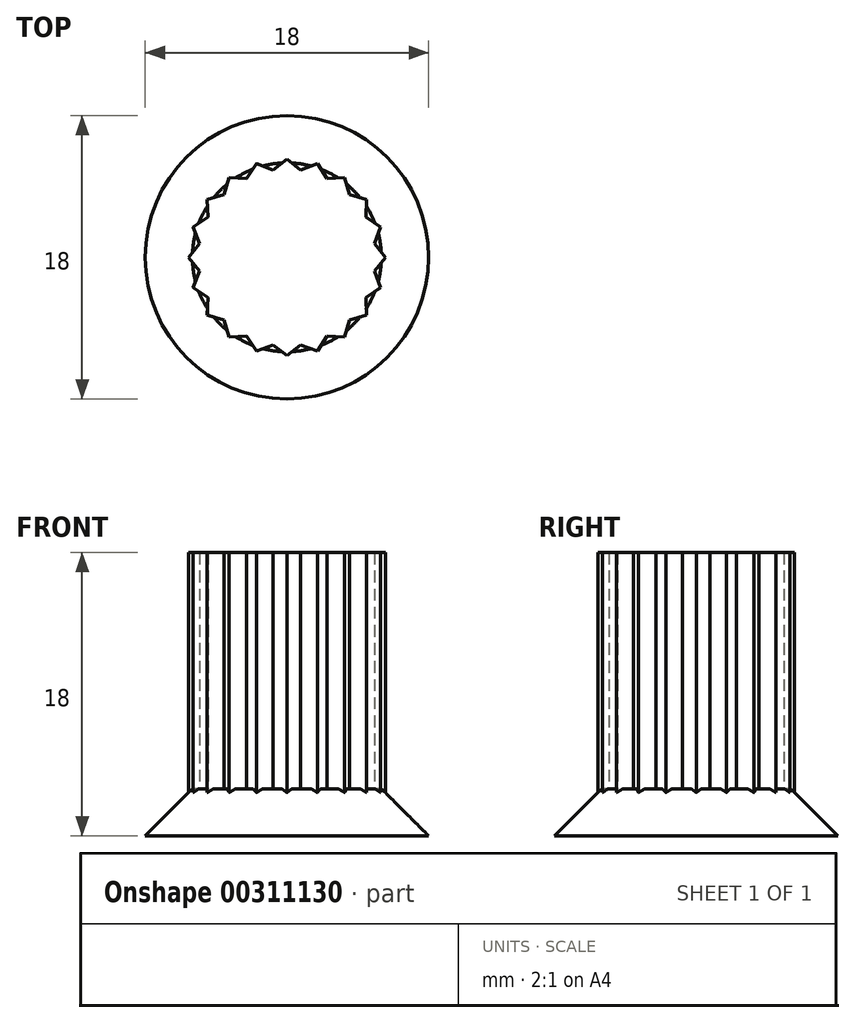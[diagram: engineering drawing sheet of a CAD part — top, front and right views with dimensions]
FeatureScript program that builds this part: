
annotation { "Feature Type Name" : "Feature", "Feature Type Description" : "" }
export const myFeature = defineFeature(function(context is Context, id is Id, definition is map)
    precondition{}
    {
        {
            var Q0;
            Q0=qCreatedBy(makeId("Top.planeOp"),FACE);
            var sketch = newSketch(context, id + "F0", { "sketchPlane" : qUnion([Q0])});
            skArc(sketch, "E0", {"start": v(0, 9) * mm, "mid": v(-6.36, 6.36) * mm, "end": v(-9, 0) * mm});
            skArc(sketch, "E1", {"start": v(-9, 0) * mm, "mid": v(-6.36, -6.36) * mm, "end": v(0, -9) * mm});
            skArc(sketch, "E2", {"start": v(0, -9) * mm, "mid": v(6.36, -6.36) * mm, "end": v(9, 0) * mm});
            skArc(sketch, "E3", {"start": v(9, 0) * mm, "mid": v(6.36, 6.36) * mm, "end": v(0, 9) * mm});
            skLineSegment(sketch, "E4", {"start": v(0.88, 5.56) * mm, "end": v(0, 6.25) * mm});
            skLineSegment(sketch, "E5", {"start": v(0, 6.25) * mm, "end": v(-0.88, 5.56) * mm});
            skLineSegment(sketch, "E6", {"start": v(-0.88, 5.56) * mm, "end": v(-1.93, 5.94) * mm});
            skLineSegment(sketch, "E7", {"start": v(-1.93, 5.94) * mm, "end": v(-2.55, 5.01) * mm});
            skLineSegment(sketch, "E8", {"start": v(-2.55, 5.01) * mm, "end": v(-3.67, 5.06) * mm});
            skLineSegment(sketch, "E9", {"start": v(-3.67, 5.06) * mm, "end": v(-3.98, 3.98) * mm});
            skLineSegment(sketch, "E10", {"start": v(-3.98, 3.98) * mm, "end": v(-5.06, 3.67) * mm});
            skLineSegment(sketch, "E11", {"start": v(-5.06, 3.67) * mm, "end": v(-5.01, 2.55) * mm});
            skLineSegment(sketch, "E12", {"start": v(-5.01, 2.55) * mm, "end": v(-5.94, 1.93) * mm});
            skLineSegment(sketch, "E13", {"start": v(-5.94, 1.93) * mm, "end": v(-5.56, 0.88) * mm});
            skLineSegment(sketch, "E14", {"start": v(-5.56, 0.88) * mm, "end": v(-6.25, 0) * mm});
            skLineSegment(sketch, "E15", {"start": v(-6.25, 0) * mm, "end": v(-5.56, -0.88) * mm});
            skLineSegment(sketch, "E16", {"start": v(-5.56, -0.88) * mm, "end": v(-5.94, -1.93) * mm});
            skLineSegment(sketch, "E17", {"start": v(-5.94, -1.93) * mm, "end": v(-5.01, -2.55) * mm});
            skLineSegment(sketch, "E18", {"start": v(-5.01, -2.55) * mm, "end": v(-5.06, -3.67) * mm});
            skLineSegment(sketch, "E19", {"start": v(-5.06, -3.67) * mm, "end": v(-3.98, -3.98) * mm});
            skLineSegment(sketch, "E20", {"start": v(-3.98, -3.98) * mm, "end": v(-3.67, -5.06) * mm});
            skLineSegment(sketch, "E21", {"start": v(-3.67, -5.06) * mm, "end": v(-2.55, -5.01) * mm});
            skLineSegment(sketch, "E22", {"start": v(-2.55, -5.01) * mm, "end": v(-1.93, -5.94) * mm});
            skLineSegment(sketch, "E23", {"start": v(-1.93, -5.94) * mm, "end": v(-0.88, -5.56) * mm});
            skLineSegment(sketch, "E24", {"start": v(-0.88, -5.56) * mm, "end": v(0, -6.25) * mm});
            skLineSegment(sketch, "E25", {"start": v(0, -6.25) * mm, "end": v(0.88, -5.56) * mm});
            skLineSegment(sketch, "E26", {"start": v(0.88, -5.56) * mm, "end": v(1.93, -5.94) * mm});
            skLineSegment(sketch, "E27", {"start": v(1.93, -5.94) * mm, "end": v(2.55, -5.01) * mm});
            skLineSegment(sketch, "E28", {"start": v(2.55, -5.01) * mm, "end": v(3.67, -5.06) * mm});
            skLineSegment(sketch, "E29", {"start": v(3.67, -5.06) * mm, "end": v(3.98, -3.98) * mm});
            skLineSegment(sketch, "E30", {"start": v(3.98, -3.98) * mm, "end": v(5.06, -3.67) * mm});
            skLineSegment(sketch, "E31", {"start": v(5.06, -3.67) * mm, "end": v(5.01, -2.55) * mm});
            skLineSegment(sketch, "E32", {"start": v(5.01, -2.55) * mm, "end": v(5.94, -1.93) * mm});
            skLineSegment(sketch, "E33", {"start": v(5.94, -1.93) * mm, "end": v(5.56, -0.88) * mm});
            skLineSegment(sketch, "E34", {"start": v(5.56, -0.88) * mm, "end": v(6.25, 0) * mm});
            skLineSegment(sketch, "E35", {"start": v(6.25, 0) * mm, "end": v(5.56, 0.88) * mm});
            skLineSegment(sketch, "E36", {"start": v(5.56, 0.88) * mm, "end": v(5.94, 1.93) * mm});
            skLineSegment(sketch, "E37", {"start": v(5.94, 1.93) * mm, "end": v(5.01, 2.55) * mm});
            skLineSegment(sketch, "E38", {"start": v(5.01, 2.55) * mm, "end": v(5.06, 3.67) * mm});
            skLineSegment(sketch, "E39", {"start": v(5.06, 3.67) * mm, "end": v(3.98, 3.98) * mm});
            skLineSegment(sketch, "E40", {"start": v(3.98, 3.98) * mm, "end": v(3.67, 5.06) * mm});
            skLineSegment(sketch, "E41", {"start": v(3.67, 5.06) * mm, "end": v(2.55, 5.01) * mm});
            skLineSegment(sketch, "E42", {"start": v(2.55, 5.01) * mm, "end": v(1.93, 5.94) * mm});
            skLineSegment(sketch, "E43", {"start": v(1.93, 5.94) * mm, "end": v(0.88, 5.56) * mm});
            skSolve(sketch);
        }
        {
            var Q0;
            Q0=makeQuery(id+"F0.imprint","IMPRINT",FACE,{"disambiguationData":[TD([[makeQuery(id+"F0.imprint","IMPRINT",EDGE,{"derivedFrom":sQuery(id+"F0.wireOp",EDGE,"E4")}),1.0]])]});
            extrude(context, id + "F1", {"entities" : qUnion([Q0]), "depth" : 18 * mm});
        }
        {
            var Q0;
            Q0=makeQuery(id+"F0.imprint","IMPRINT",FACE,{"disambiguationData":[TD([[makeQuery(id+"F0.imprint","IMPRINT",EDGE,{"derivedFrom":sQuery(id+"F0.wireOp",EDGE,"E0")}),1.0]])]});
            extrude(context, id + "F2", {"entities" : qUnion([Q0]), "operationType" : NewBodyOperationType.ADD, "depth" : 3 * mm});
        }
        {
            var Q0;
            Q0=makeQuery(id+"F2.opExtrude","CAP_EDGE",EDGE,{"disambiguationData":[OSD([sQuery(id+"F0.wireOp",EDGE,"E0"),sQuery(id+"F0.wireOp",EDGE,"E1"),sQuery(id+"F0.wireOp",EDGE,"E2"),sQuery(id+"F0.wireOp",EDGE,"E3")])],"isStart":false});
            chamfer(context, id + "F3", {"entities" : qUnion([Q0]), "width" : 3 * mm, "tangentPropagation" : true});
        }
    });
